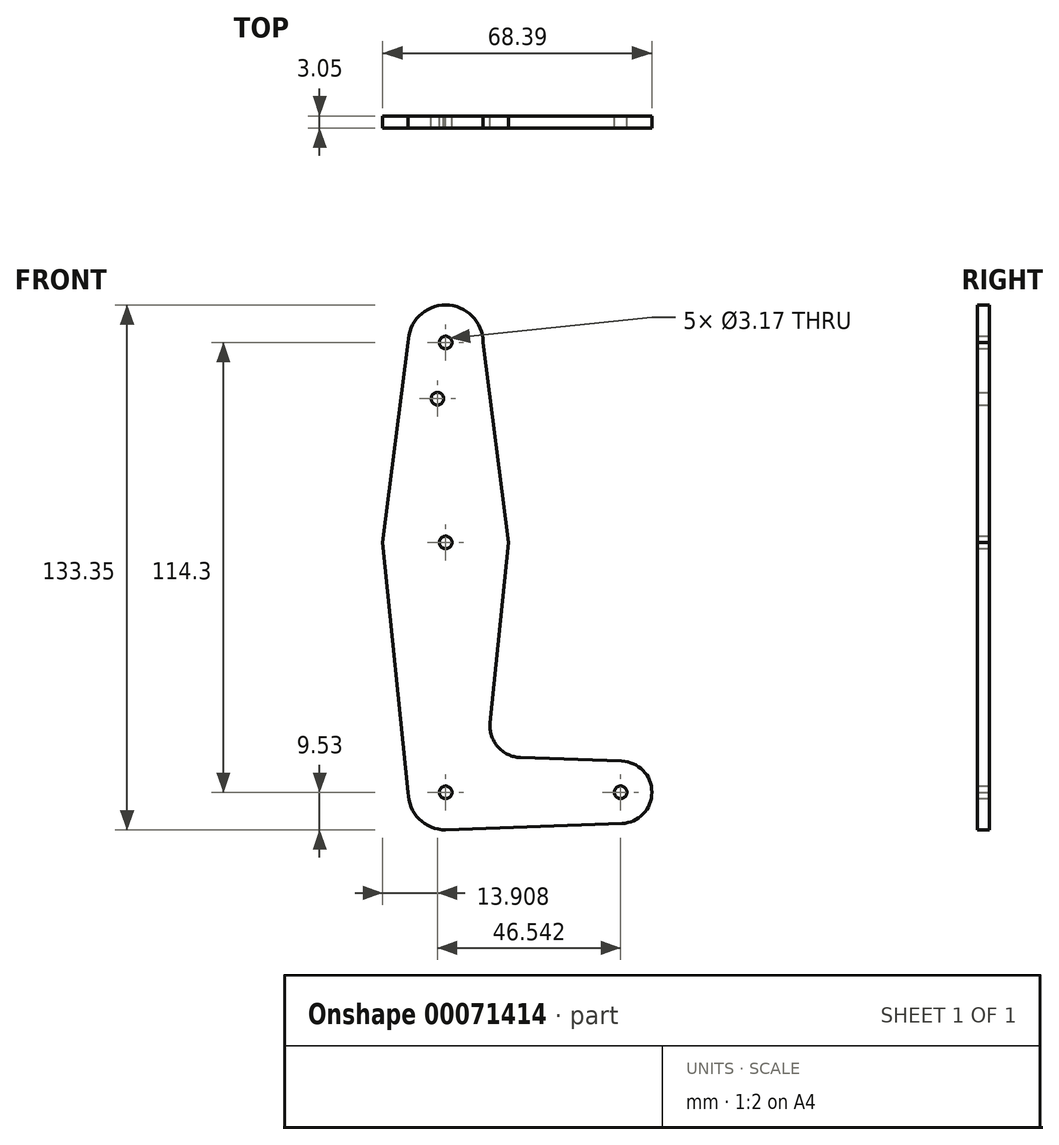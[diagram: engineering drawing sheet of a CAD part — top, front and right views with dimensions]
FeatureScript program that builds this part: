
annotation { "Feature Type Name" : "Feature", "Feature Type Description" : "" }
export const myFeature = defineFeature(function(context is Context, id is Id, definition is map)
    precondition{}
    {
        {
            var Q0;
            Q0=qCreatedBy(makeId("Front.planeOp"),FACE);
            var sketch = newSketch(context, id + "F0", { "sketchPlane" : qUnion([Q0])});
            skCircle(sketch, "E0", {"center": v(0, 0) * mm, "radius": 15.88 * mm});
            skCircle(sketch, "E1", {"center": v(0, -63.5) * mm, "radius": 9.53 * mm});
            skCircle(sketch, "E2", {"center": v(44.45, -63.47) * mm, "radius": 7.94 * mm});
            skCircle(sketch, "E3", {"center": v(0, 50.8) * mm, "radius": 9.53 * mm});
            skLineSegment(sketch, "E4", {"start": v(-9.52, -63.5) * mm, "end": v(-16, 0) * mm});
            skLineSegment(sketch, "E5", {"start": v(11.32, -45.88) * mm, "end": v(16, 0) * mm});
            skLineSegment(sketch, "E6", {"start": v(-9.53, 50.8) * mm, "end": v(-16, 0) * mm});
            skLineSegment(sketch, "E7", {"start": v(9.53, 50.8) * mm, "end": v(16, 0) * mm});
            skLineSegment(sketch, "E8", {"start": v(0, -73.03) * mm, "end": v(44.74, -71.4) * mm});
            skLineSegment(sketch, "E9", {"start": v(0, -63.5) * mm, "end": v(44.45, -63.47) * mm, "construction": true});
            skLineSegment(sketch, "E10", {"start": v(0, -63.5) * mm, "end": v(0, 0) * mm, "construction": true});
            skCircle(sketch, "E11", {"center": v(0, 0) * mm, "radius": 1.59 * mm});
            skCircle(sketch, "E12", {"center": v(0, 50.8) * mm, "radius": 1.59 * mm});
            skCircle(sketch, "E13", {"center": v(0, -63.5) * mm, "radius": 1.59 * mm});
            skCircle(sketch, "E14", {"center": v(44.45, -63.47) * mm, "radius": 1.59 * mm});
            skCircle(sketch, "E15", {"center": v(-2.1, 36.53) * mm, "radius": 1.59 * mm});
            skLineSegment(sketch, "E16", {"start": v(0, 0) * mm, "end": v(0, 33.35) * mm});
            skLineSegment(sketch, "E17", {"start": v(18.95, -54.64) * mm, "end": v(44.73, -55.54) * mm});
            skPoint(sketch, "E18.newPointA", {"position": v(9.53, -63.5) * mm});
            skArc(sketch, "E18.filletArc", {"start": v(11.32, -45.88) * mm, "mid": v(13.24, -51.92) * mm, "end": v(18.95, -54.64) * mm});
            skSolve(sketch);
        }
        {
            var Q0;
            Q0=makeQuery(id+"F0.imprint","IMPRINT",FACE,{"disambiguationData":[TD([[makeQuery(id+"F0.imprint","IMPRINT",EDGE,{"derivedFrom":sQuery(id+"F0.wireOp",EDGE,"E11")}),-1.0]])]});
            var Q1;
            Q1=makeQuery(id+"F0.imprint","IMPRINT",FACE,{"disambiguationData":[TD([[makeQuery(id+"F0.imprint","IMPRINT",EDGE,{"derivedFrom":sQuery(id+"F0.wireOp",EDGE,"E14")}),-1.0]])]});
            var Q2;
            Q2=makeQuery(id+"F0.imprint","IMPRINT",FACE,{"disambiguationData":[TD([[makeQuery(id+"F0.imprint","IMPRINT",EDGE,{"derivedFrom":sQuery(id+"F0.wireOp",EDGE,"E13")}),-1.0]])]});
            var Q3;
            Q3=makeQuery(id+"F0.imprint","IMPRINT",FACE,{"disambiguationData":[TD([[makeQuery(id+"F0.imprint","IMPRINT",EDGE,{"derivedFrom":sQuery(id+"F0.wireOp",EDGE,"E12")}),-1.0]])]});
            var Q4;
            {var subQ4=sQuery(id+"F0.wireOp",EDGE,"E4");Q4=makeQuery(id+"F0.imprint","IMPRINT",FACE,{"disambiguationData":[TD([[makeQuery(id+"F0.imprint","IMPRINT",EDGE,{"derivedFrom":subQ4}),-1.0]])]});}
            extrude(context, id + "F1", {"entities" : qUnion([Q0, Q1, Q2, Q3, Q4]), "depth" : 3.05 * mm});
        }
    });
